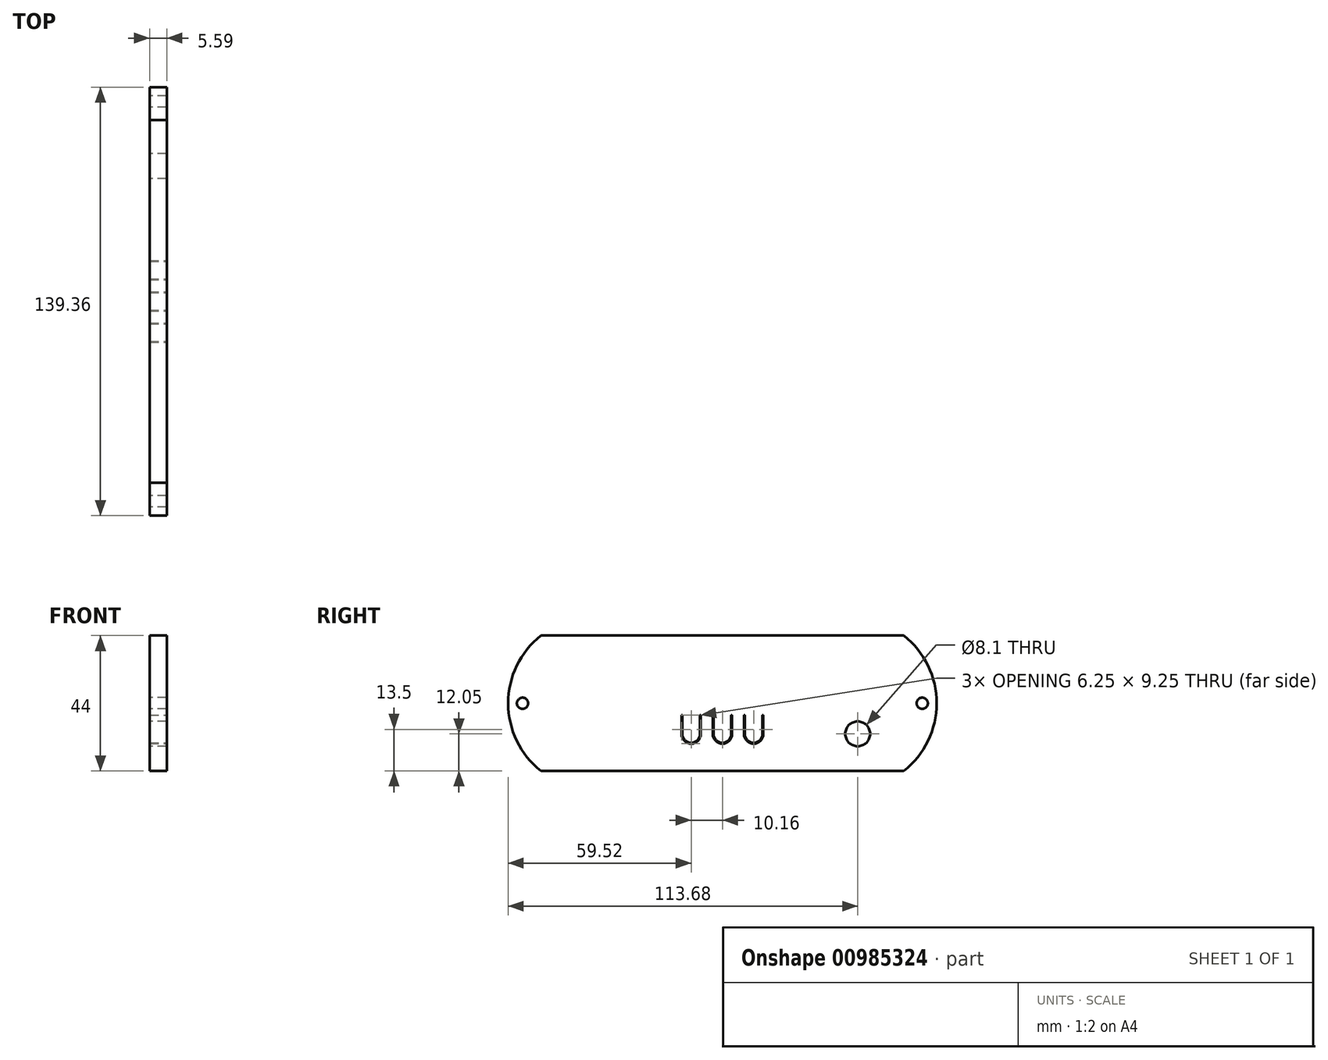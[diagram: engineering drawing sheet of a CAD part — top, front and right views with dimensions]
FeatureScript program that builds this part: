
annotation { "Feature Type Name" : "Feature", "Feature Type Description" : "" }
export const myFeature = defineFeature(function(context is Context, id is Id, definition is map)
    precondition{}
    {
        {
            var Q0;
            Q0=qCreatedBy(makeId("Right.planeOp"),FACE);
            var sketch = newSketch(context, id + "F0", { "sketchPlane" : qUnion([Q0])});
            skLineSegment(sketch, "E0.rect.bottom", {"start": v(59, 22) * mm, "end": v(-59, 22) * mm});
            skLineSegment(sketch, "E0.rect.top", {"start": v(59, -22) * mm, "end": v(-59, -22) * mm});
            skLineSegment(sketch, "E0.rect.left", {"start": v(59, 22) * mm, "end": v(59, -22) * mm, "construction": true});
            skLineSegment(sketch, "E0.rect.right", {"start": v(-59, 22) * mm, "end": v(-59, -22) * mm, "construction": true});
            skPoint(sketch, "E0.rect.middle", {"position": v(0, 0) * mm});
            skLineSegment(sketch, "E1", {"start": v(-59, 0) * mm, "end": v(59, 0) * mm, "construction": true});
            skArc(sketch, "E2", {"start": v(-59, 22) * mm, "mid": v(-69.68, 0) * mm, "end": v(-59, -22) * mm});
            skArc(sketch, "E3", {"start": v(59, -22) * mm, "mid": v(69.68, 0) * mm, "end": v(59, 22) * mm});
            skCircle(sketch, "E4", {"center": v(-65, 0) * mm, "radius": 1.83 * mm});
            skCircle(sketch, "E5", {"center": v(65, 0) * mm, "radius": 1.83 * mm});
            skCircle(sketch, "E6", {"center": v(44, -9.95) * mm, "radius": 4.05 * mm});
            skSolve(sketch);
        }
        {
            var Q0;
            Q0=makeQuery(id+"F0.imprint","IMPRINT",FACE,{"disambiguationData":[TD([[makeQuery(id+"F0.imprint","IMPRINT",EDGE,{"derivedFrom":sQuery(id+"F0.wireOp",EDGE,"E0.rect.bottom")}),1.0]])]});
            extrude(context, id + "F1", {"entities" : qUnion([Q0]), "depth" : 5.6 * mm});
        }
        {
            var Q0;
            Q0=makeQuery(id+"F1.opExtrude","CAP_FACE",FACE,{"disambiguationData":[OSD([sQuery(id+"F0.wireOp",EDGE,"E0.rect.bottom"),sQuery(id+"F0.wireOp",EDGE,"E0.rect.top"),sQuery(id+"F0.wireOp",EDGE,"E2"),sQuery(id+"F0.wireOp",EDGE,"E3"),sQuery(id+"F0.wireOp",EDGE,"E4"),sQuery(id+"F0.wireOp",EDGE,"E5"),sQuery(id+"F0.wireOp",EDGE,"E6")])],"isStart":false});
            var sketch = newSketch(context, id + "F2", { "sketchPlane" : qUnion([Q0])});
            skLineSegment(sketch, "E7", {"start": v(7.16, -4) * mm, "end": v(7.16, -10) * mm, "construction": true});
            skArc(sketch, "E8", {"start": v(7.16, -10) * mm, "mid": v(10.16, -13) * mm, "end": v(13.16, -10) * mm, "construction": true});
            skLineSegment(sketch, "E9", {"start": v(13.16, -10) * mm, "end": v(13.16, -4) * mm, "construction": true});
            skArc(sketch, "E10.0.startCap", {"start": v(7.03, -4) * mm, "mid": v(7.16, -3.87) * mm, "end": v(7.29, -4) * mm});
            skLineSegment(sketch, "E10.0.left", {"start": v(7.29, -4) * mm, "end": v(7.29, -10) * mm});
            skLineSegment(sketch, "E10.0.right", {"start": v(7.03, -4) * mm, "end": v(7.03, -10) * mm});
            skArc(sketch, "E10.1.left", {"start": v(7.29, -10) * mm, "mid": v(10.16, -12.87) * mm, "end": v(13.03, -10) * mm});
            skArc(sketch, "E10.1.right", {"start": v(7.03, -10) * mm, "mid": v(10.16, -13.13) * mm, "end": v(13.29, -10) * mm});
            skArc(sketch, "E10.2.endCap", {"start": v(13.03, -4) * mm, "mid": v(13.16, -3.87) * mm, "end": v(13.29, -4) * mm});
            skLineSegment(sketch, "E10.2.left", {"start": v(13.03, -10) * mm, "end": v(13.03, -4) * mm});
            skLineSegment(sketch, "E10.2.right", {"start": v(13.29, -10) * mm, "end": v(13.29, -4) * mm});
            skArc(sketch, "E11.1.0.0", {"start": v(-2.87, -10) * mm, "mid": v(0, -12.87) * mm, "end": v(2.87, -10) * mm});
            skLineSegment(sketch, "E11.1.0.1", {"start": v(3.13, -10) * mm, "end": v(3.13, -4) * mm});
            skLineSegment(sketch, "E11.1.0.2", {"start": v(2.87, -10) * mm, "end": v(2.87, -4) * mm});
            skArc(sketch, "E11.1.0.3", {"start": v(-3.13, -10) * mm, "mid": v(0, -13.13) * mm, "end": v(3.13, -10) * mm});
            skLineSegment(sketch, "E11.1.0.4", {"start": v(-2.87, -4) * mm, "end": v(-2.87, -10) * mm});
            skLineSegment(sketch, "E11.1.0.5", {"start": v(-3.13, -4) * mm, "end": v(-3.13, -10) * mm});
            skArc(sketch, "E11.1.0.6", {"start": v(-3.13, -4) * mm, "mid": v(-3, -3.87) * mm, "end": v(-2.87, -4) * mm});
            skArc(sketch, "E11.1.0.7", {"start": v(2.87, -4) * mm, "mid": v(3, -3.87) * mm, "end": v(3.13, -4) * mm});
            skArc(sketch, "E11.2.0.0", {"start": v(-13.03, -10) * mm, "mid": v(-10.16, -12.87) * mm, "end": v(-7.29, -10) * mm});
            skLineSegment(sketch, "E11.2.0.1", {"start": v(-7.03, -10) * mm, "end": v(-7.03, -4) * mm});
            skLineSegment(sketch, "E11.2.0.2", {"start": v(-7.29, -10) * mm, "end": v(-7.29, -4) * mm});
            skArc(sketch, "E11.2.0.3", {"start": v(-13.29, -10) * mm, "mid": v(-10.16, -13.13) * mm, "end": v(-7.03, -10) * mm});
            skLineSegment(sketch, "E11.2.0.4", {"start": v(-13.03, -4) * mm, "end": v(-13.03, -10) * mm});
            skLineSegment(sketch, "E11.2.0.5", {"start": v(-13.29, -4) * mm, "end": v(-13.29, -10) * mm});
            skArc(sketch, "E11.2.0.6", {"start": v(-13.29, -4) * mm, "mid": v(-13.16, -3.87) * mm, "end": v(-13.03, -4) * mm});
            skArc(sketch, "E11.2.0.7", {"start": v(-7.29, -4) * mm, "mid": v(-7.16, -3.87) * mm, "end": v(-7.03, -4) * mm});
            skLineSegment(sketch, "E11.direction1", {"start": v(7.03, -10) * mm, "end": v(-3.13, -10) * mm, "construction": true});
            skSolve(sketch);
        }
        {
            var Q0;
            Q0=qSketchRegion(id+"F2",true);
            extrude(context, id + "F3", {"entities" : qUnion([Q0]), "operationType" : NewBodyOperationType.REMOVE, "endBound" : BoundingType.UP_TO_NEXT, "oppositeDirection" : true, "depth" : 25 * mm});
        }
    });
